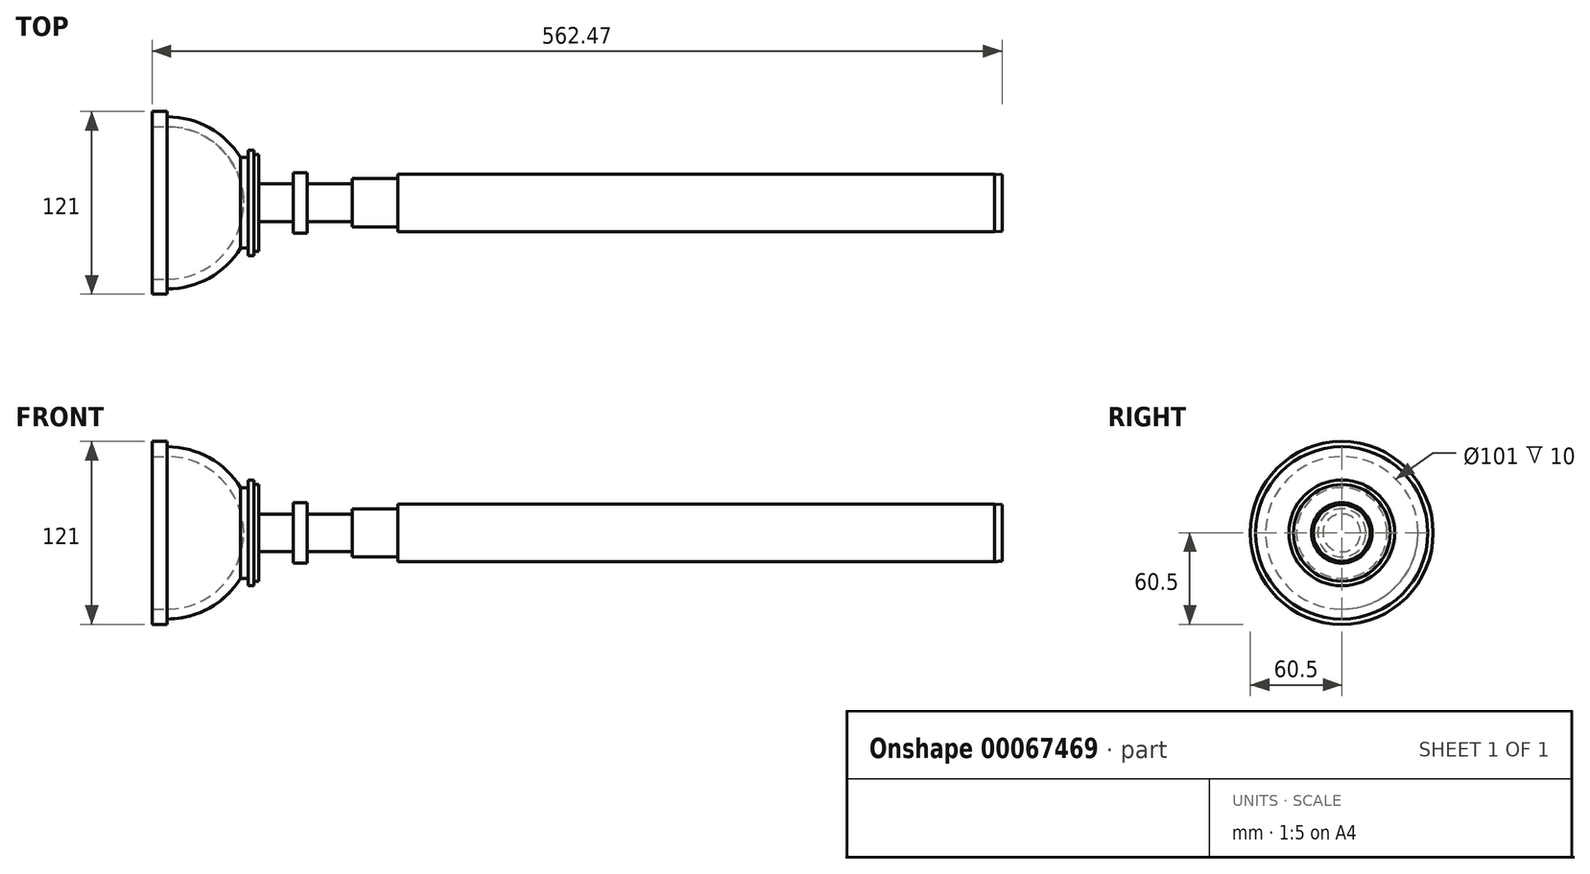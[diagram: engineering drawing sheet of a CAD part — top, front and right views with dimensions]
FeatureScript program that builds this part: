
annotation { "Feature Type Name" : "Feature", "Feature Type Description" : "" }
export const myFeature = defineFeature(function(context is Context, id is Id, definition is map)
    precondition{}
    {
        {
            assignVariable(context, id + "F0", {"name" : "s", "anyValue" : 1});
        }
        {
            var Q0;
            Q0=qCreatedBy(makeId("Top.planeOp"),FACE);
            var sketch = newSketch(context, id + "F1", { "sketchPlane" : qUnion([Q0])});
            skPoint(sketch, "E0.visualSharp", {"position": v(-547.47, 57) * mm});
            skLineSegment(sketch, "E1", {"start": v(0, 0) * mm, "end": v(-496.97, 0) * mm});
            skLineSegment(sketch, "E2", {"start": v(0, 19) * mm, "end": v(-395, 19) * mm});
            skArc(sketch, "E3", {"start": v(-496.97, 0) * mm, "mid": v(-511.76, 35.7) * mm, "end": v(-547.47, 50.5) * mm});
            skArc(sketch, "E4", {"start": v(-499, 30) * mm, "mid": v(-519.73, 49.8) * mm, "end": v(-547.47, 57) * mm});
            skLineSegment(sketch, "E5", {"start": v(-425, 12.5) * mm, "end": v(-455, 12.5) * mm});
            skLineSegment(sketch, "E6", {"start": v(0, 19) * mm, "end": v(0, 0) * mm});
            skLineSegment(sketch, "E7", {"start": v(-557.47, 60.5) * mm, "end": v(-557.47, 50.5) * mm});
            skLineSegment(sketch, "E8", {"start": v(-395, 16) * mm, "end": v(-425, 16) * mm});
            skLineSegment(sketch, "E9", {"start": v(-395, 19) * mm, "end": v(-395, 16) * mm});
            skLineSegment(sketch, "E10", {"start": v(-547.47, 60.5) * mm, "end": v(-557.47, 60.5) * mm});
            skLineSegment(sketch, "E11", {"start": v(-557.47, 50.5) * mm, "end": v(-547.47, 50.5) * mm});
            skLineSegment(sketch, "E12", {"start": v(-464, 20) * mm, "end": v(-464, 12.5) * mm});
            skLineSegment(sketch, "E13", {"start": v(-487, 12.5) * mm, "end": v(-487, 32) * mm});
            skLineSegment(sketch, "E14", {"start": v(-464, 12.5) * mm, "end": v(-487, 12.5) * mm});
            skLineSegment(sketch, "E15", {"start": v(-425, 16) * mm, "end": v(-425, 12.5) * mm});
            skLineSegment(sketch, "E16", {"start": v(-455, 12.5) * mm, "end": v(-455, 20) * mm});
            skLineSegment(sketch, "E17", {"start": v(-455, 20) * mm, "end": v(-464, 20) * mm});
            skLineSegment(sketch, "E18", {"start": v(-547.47, 57) * mm, "end": v(-547.47, 60.5) * mm});
            skLineSegment(sketch, "E19", {"start": v(-487, 32) * mm, "end": v(-490, 32) * mm});
            skLineSegment(sketch, "E20", {"start": v(-490, 35) * mm, "end": v(-494, 35) * mm});
            skLineSegment(sketch, "E21", {"start": v(-494, 30) * mm, "end": v(-499, 30) * mm});
            skLineSegment(sketch, "E22", {"start": v(-490, 32) * mm, "end": v(-490, 35) * mm});
            skLineSegment(sketch, "E23", {"start": v(-494, 35) * mm, "end": v(-494, 30) * mm});
            skSolve(sketch);
        }
        {
            var Q0;
            Q0 = qSketchRegion(id + "F1", true);
            var Q1;
            Q1=sQuery(id+"F1.wireOp",EDGE,"E1");
            revolve(context, id + "F2", {"entities" : qUnion([Q0]), "axis" : qUnion([Q1]), "revolveType" : RevolveType.FULL});
        }
        {
            var Q0;
            Q0=makeQuery(id+"F2.opRevolve","SWEPT_FACE",FACE,{"disambiguationData":[OSD([sQuery(id+"F1.wireOp",EDGE,"E6")])]});
            extrude(context, id + "F3", {"entities" : qUnion([Q0]), "operationType" : NewBodyOperationType.ADD, "depth" : (5 * getVariable(context, 's')) * mm, "hasDraft" : true, "draftAngle" : 3 * degree, "draftPullDirection" : true});
        }
        {
            assignVariable(context, id + "F4", {"name" : "scale", "anyValue" : 1});
        }
        {
            var Q0;
            Q0=makeQuery(id+"F2.opRevolve","SWEPT_BODY",BODY,{"disambiguationData":[OSD([sQuery(id+"F1.wireOp",EDGE,"E1"),sQuery(id+"F1.wireOp",EDGE,"E2"),sQuery(id+"F1.wireOp",EDGE,"E3"),sQuery(id+"F1.wireOp",EDGE,"E4"),sQuery(id+"F1.wireOp",EDGE,"E5"),sQuery(id+"F1.wireOp",EDGE,"E6"),sQuery(id+"F1.wireOp",EDGE,"E7"),sQuery(id+"F1.wireOp",EDGE,"E8"),sQuery(id+"F1.wireOp",EDGE,"E9"),sQuery(id+"F1.wireOp",EDGE,"E10"),sQuery(id+"F1.wireOp",EDGE,"E11"),sQuery(id+"F1.wireOp",EDGE,"E12"),sQuery(id+"F1.wireOp",EDGE,"E13"),sQuery(id+"F1.wireOp",EDGE,"E14"),sQuery(id+"F1.wireOp",EDGE,"E15"),sQuery(id+"F1.wireOp",EDGE,"E16"),sQuery(id+"F1.wireOp",EDGE,"E17"),sQuery(id+"F1.wireOp",EDGE,"E18"),sQuery(id+"F1.wireOp",EDGE,"E19"),sQuery(id+"F1.wireOp",EDGE,"E20"),sQuery(id+"F1.wireOp",EDGE,"E21"),sQuery(id+"F1.wireOp",EDGE,"E22"),sQuery(id+"F1.wireOp",EDGE,"E23")])]});
            var Q1;
            Q1=qCreatedBy(makeId("Origin.pointOp"),VERTEX);
            transform(context, id + "F5", {"entities" : qUnion([Q0]), "transformType" : TransformType.SCALE_UNIFORMLY, "scale" : getVariable(context, 'scale'), "scalePoint" : qUnion([Q1]), "makeCopy" : false});
        }
    });
